# Revit family: holyoake-lr-fire-damper 300
name_source: partatom
category: Duct Accessories
units: mm (PartAtom-declared; Revit-internal decimal feet)

## family parameters
Always vertical = No
Cut with Voids When Loaded = No
Part Type = Breaks Into
Round Connector Dimension = Use Diameter
Shared = No
Work Plane-Based = No

## types (5) — shared parameters
Description = LR Fire / Combination Fire and Smoke Dampers
Heat Shield = No
Length = 425 mm  [stored 1.39436 ft]
Manufacturer = Holyoake
Material - Body = <By Category>
Material - Flange = <By Category>
URL = http://www.holyoake.com
zero-valued in all types: Default Elevation

## per-type parameters (varying)
| type | Fire Smoke Actuator | Wall Thickness Maximum |
| FSH | No | 295 mm |
| FSO | Yes | 210 mm |
| FH | No | 210 mm |
| FO | No | 295 mm |
| Holyoake LR | No | 210 mm |

note: [stored X ft] marks values corroborated as IEEE doubles in the binary element streams (Revit-internal decimal feet)

## geometry (parser evidence)
native form markers: Blend x4, Sweep x9
no freeform markers — native parametric forms only
